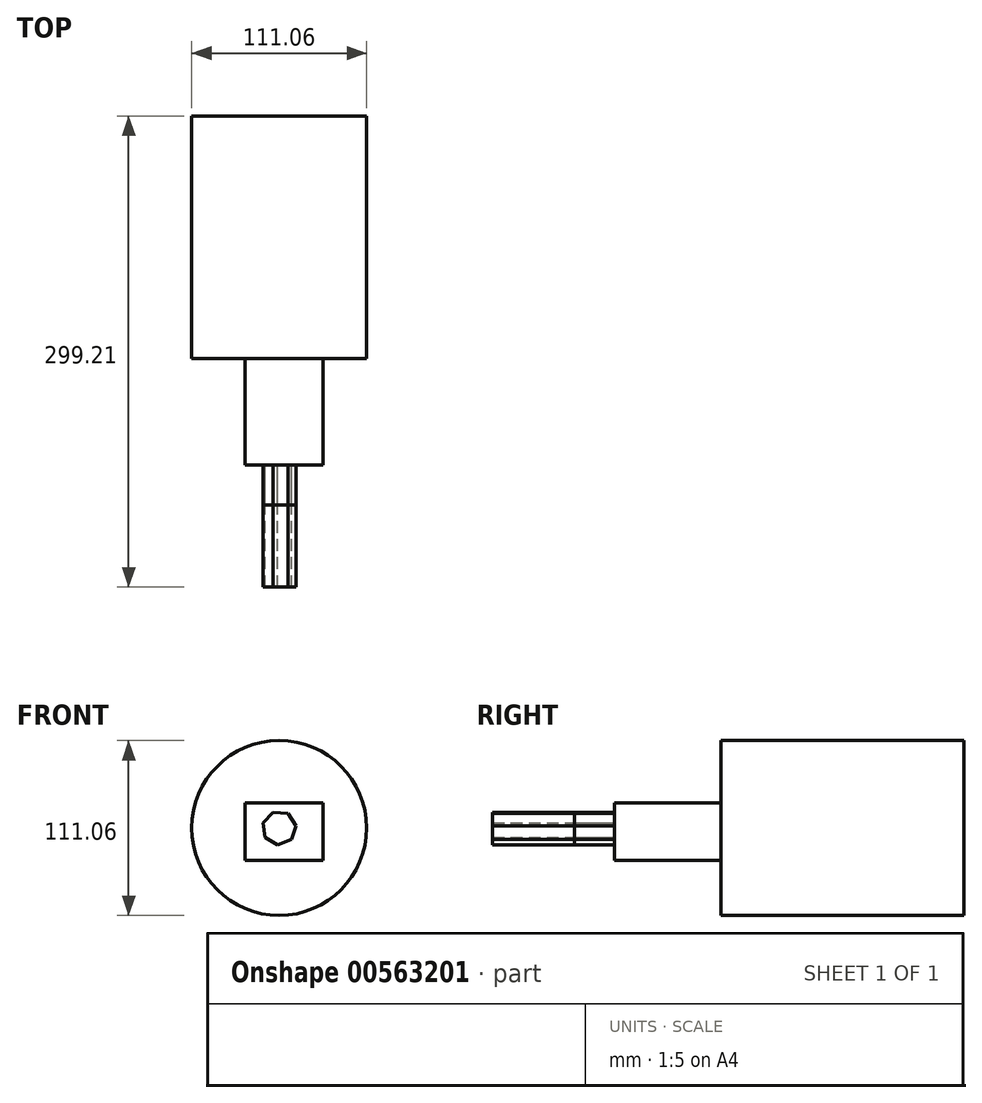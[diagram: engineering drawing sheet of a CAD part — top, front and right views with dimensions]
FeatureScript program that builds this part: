
annotation { "Feature Type Name" : "Feature", "Feature Type Description" : "" }
export const myFeature = defineFeature(function(context is Context, id is Id, definition is map)
    precondition{}
    {
        {
            var Q0;
            Q0=qCreatedBy(makeId("Front.planeOp"),FACE);
            var sketch = newSketch(context, id + "F0", { "sketchPlane" : qUnion([Q0])});
            skCircle(sketch, "E0", {"center": v(0, 0) * mm, "radius": 55.53 * mm});
            skSolve(sketch);
        }
        {
            var Q0;
            Q0 = qSketchRegion(id + "F0", true);
            extrude(context, id + "F1", {"entities" : qUnion([Q0]), "depth" : 154.18 * mm, "offsetDistance" : 25.4 * mm});
        }
        {
            var Q0;
            Q0=makeQuery(id+"F1.opExtrude","CAP_FACE",FACE,{"disambiguationData":[OSD([sQuery(id+"F0.wireOp",EDGE,"E0")])],"isStart":false});
            var sketch = newSketch(context, id + "F2", { "sketchPlane" : qUnion([Q0])});
            skLineSegment(sketch, "E1.bottom", {"start": v(-21.62, 16) * mm, "end": v(27.8, 16) * mm});
            skLineSegment(sketch, "E1.top", {"start": v(-21.62, -20.5) * mm, "end": v(27.8, -20.5) * mm});
            skLineSegment(sketch, "E1.left", {"start": v(-21.62, 16) * mm, "end": v(-21.62, -20.5) * mm});
            skLineSegment(sketch, "E1.right", {"start": v(27.8, 16) * mm, "end": v(27.8, -20.5) * mm});
            skSolve(sketch);
        }
        {
            var Q0;
            Q0 = qSketchRegion(id + "F2", true);
            extrude(context, id + "F3", {"entities" : qUnion([Q0]), "operationType" : NewBodyOperationType.ADD, "depth" : 67.56 * mm, "offsetDistance" : 25.4 * mm});
        }
        {
            var Q0;
            Q0=makeQuery(id+"F3.opExtrude","CAP_FACE",FACE,{"disambiguationData":[OSD([sQuery(id+"F2.wireOp",EDGE,"E1.bottom"),sQuery(id+"F2.wireOp",EDGE,"E1.top"),sQuery(id+"F2.wireOp",EDGE,"E1.left"),sQuery(id+"F2.wireOp",EDGE,"E1.right")])],"isStart":false});
            var sketch = newSketch(context, id + "F4", { "sketchPlane" : qUnion([Q0])});
            skCircle(sketch, "E2.cCircle", {"center": v(0, 0) * mm, "radius": 9.6 * mm, "construction": true});
            skLineSegment(sketch, "E2.0", {"start": v(7.7, -7.36) * mm, "end": v(-0.96, -10.6) * mm});
            skLineSegment(sketch, "E2.1", {"start": v(-0.96, -10.6) * mm, "end": v(-8.89, -5.86) * mm});
            skLineSegment(sketch, "E2.2", {"start": v(-8.89, -5.86) * mm, "end": v(-10.13, 3.3) * mm});
            skLineSegment(sketch, "E2.3", {"start": v(-10.13, 3.3) * mm, "end": v(-3.74, 9.97) * mm});
            skLineSegment(sketch, "E2.4", {"start": v(-3.74, 9.97) * mm, "end": v(5.46, 9.14) * mm});
            skLineSegment(sketch, "E2.5", {"start": v(5.46, 9.14) * mm, "end": v(10.55, 1.43) * mm});
            skLineSegment(sketch, "E2.6", {"start": v(10.55, 1.43) * mm, "end": v(7.7, -7.36) * mm});
            skPoint(sketch, "E2.0.midPoint", {"position": v(3.37, -8.98) * mm});
            skSolve(sketch);
        }
        {
            var Q0;
            Q0 = qSketchRegion(id + "F4", true);
            extrude(context, id + "F5", {"entities" : qUnion([Q0]), "depth" : 25.4 * mm, "offsetDistance" : 25.4 * mm});
        }
        {
            var Q0;
            Q0 = qSketchRegion(id + "F4", true);
            extrude(context, id + "F6", {"entities" : qUnion([Q0]), "depth" : 77.47 * mm, "offsetDistance" : 25.4 * mm});
        }
    });
